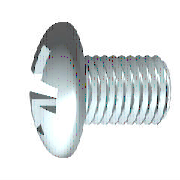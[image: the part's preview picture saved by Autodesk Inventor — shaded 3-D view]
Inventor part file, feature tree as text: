
AUTODESK INVENTOR PART (.ipt)
format: ipt  version: 2022 (Build 260153000, 153)  size: 275,456 bytes
history: native  units: mm (DEFAULTED — no unit token found)
features: other x2, plane x2, extrude x1
ambient origin geometry x7: Origin, YZ Plane, XZ Plane, X Axis, Y Axis, Z Axis, Center Point
bodies: Solid1 (feature_tree)
feature tree (5):
  other  "Базовый элемент"
  plane  "Work Plane1"
  extrude  "Паз"  Depth=3.5mm
  other  "Вырез"
  plane  "Work Plane3"
